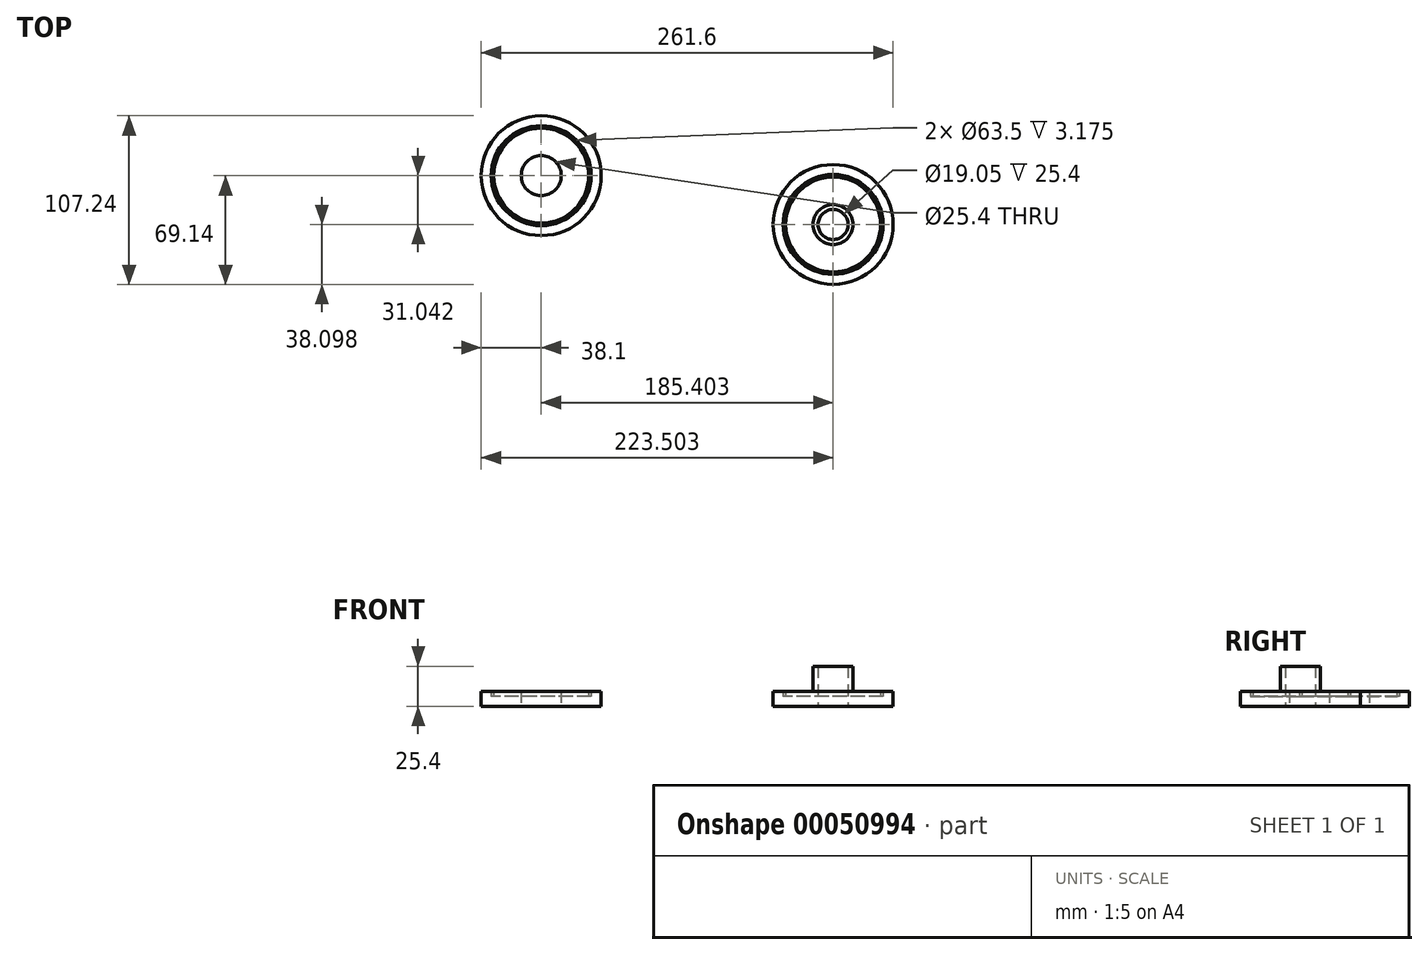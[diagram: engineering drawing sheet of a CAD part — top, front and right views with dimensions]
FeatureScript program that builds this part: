
annotation { "Feature Type Name" : "Feature", "Feature Type Description" : "" }
export const myFeature = defineFeature(function(context is Context, id is Id, definition is map)
    precondition{}
    {
        {
            var Q0;
            Q0=qCreatedBy(makeId("Top.planeOp"),FACE);
            var sketch = newSketch(context, id + "F0", { "sketchPlane" : qUnion([Q0])});
            skCircle(sketch, "E0", {"center": v(0, 0) * mm, "radius": 38.1 * mm});
            skCircle(sketch, "E1", {"center": v(0, 0) * mm, "radius": 31.75 * mm});
            skCircle(sketch, "E2", {"center": v(0, 0) * mm, "radius": 30.15 * mm});
            skCircle(sketch, "E3", {"center": v(0, 0) * mm, "radius": 12.7 * mm});
            skSolve(sketch);
        }
        {
            var Q0;
            Q0 = qSketchRegion(id + "F0", true);
            var Q1;
            Q1=makeQuery(id+"F0.imprint","IMPRINT",FACE,{"disambiguationData":[TD([[makeQuery(id+"F0.imprint","IMPRINT",EDGE,{"derivedFrom":sQuery(id+"F0.wireOp",EDGE,"E1")}),1.0]])]});
            var Q2;
            Q2=makeQuery(id+"F0.imprint","IMPRINT",FACE,{"disambiguationData":[TD([[makeQuery(id+"F0.imprint","IMPRINT",EDGE,{"derivedFrom":sQuery(id+"F0.wireOp",EDGE,"E2")}),1.0]])]});
            extrude(context, id + "F1", {"entities" : qUnion([Q0, Q1, Q2]), "depth" : 6.35 * mm});
        }
        {
            var Q0;
            Q0 = qSketchRegion(id + "F0", true);
            var Q1;
            Q1=makeQuery(id+"F0.imprint","IMPRINT",FACE,{"disambiguationData":[TD([[makeQuery(id+"F0.imprint","IMPRINT",EDGE,{"derivedFrom":sQuery(id+"F0.wireOp",EDGE,"E2")}),1.0]])]});
            extrude(context, id + "F2", {"entities" : qUnion([Q0, Q1]), "operationType" : NewBodyOperationType.ADD, "depth" : 9.52 * mm});
        }
        {
            var Q0;
            Q0=qCreatedBy(makeId("Top.planeOp"),FACE);
            var sketch = newSketch(context, id + "F3", { "sketchPlane" : qUnion([Q0])});
            skCircle(sketch, "E4", {"center": v(185.4, -31.04) * mm, "radius": 38.1 * mm});
            skCircle(sketch, "E5", {"center": v(185.4, -31.04) * mm, "radius": 31.75 * mm});
            skCircle(sketch, "E6", {"center": v(185.4, -31.04) * mm, "radius": 30.15 * mm});
            skCircle(sketch, "E7", {"center": v(185.4, -31.04) * mm, "radius": 12.7 * mm});
            skCircle(sketch, "E8", {"center": v(185.4, -31.04) * mm, "radius": 9.53 * mm});
            skSolve(sketch);
        }
        {
            var Q0;
            Q0=makeQuery(id+"F3.imprint","IMPRINT",FACE,{"disambiguationData":[TD([[makeQuery(id+"F3.imprint","IMPRINT",EDGE,{"derivedFrom":sQuery(id+"F3.wireOp",EDGE,"E5")}),1.0]])]});
            var Q1;
            Q1=makeQuery(id+"F3.imprint","IMPRINT",FACE,{"disambiguationData":[TD([[makeQuery(id+"F3.imprint","IMPRINT",EDGE,{"derivedFrom":sQuery(id+"F3.wireOp",EDGE,"E6")}),1.0]])]});
            var Q2;
            Q2=makeQuery(id+"F3.imprint","IMPRINT",FACE,{"disambiguationData":[TD([[makeQuery(id+"F3.imprint","IMPRINT",EDGE,{"derivedFrom":sQuery(id+"F3.wireOp",EDGE,"E4")}),1.0]])]});
            extrude(context, id + "F4", {"entities" : qUnion([Q0, Q1, Q2]), "depth" : 6.35 * mm});
        }
        {
            var Q0;
            Q0=makeQuery(id+"F3.imprint","IMPRINT",FACE,{"disambiguationData":[TD([[makeQuery(id+"F3.imprint","IMPRINT",EDGE,{"derivedFrom":sQuery(id+"F3.wireOp",EDGE,"E6")}),1.0]])]});
            var Q1;
            Q1=makeQuery(id+"F3.imprint","IMPRINT",FACE,{"disambiguationData":[TD([[makeQuery(id+"F3.imprint","IMPRINT",EDGE,{"derivedFrom":sQuery(id+"F3.wireOp",EDGE,"E4")}),1.0]])]});
            extrude(context, id + "F5", {"entities" : qUnion([Q0, Q1]), "operationType" : NewBodyOperationType.ADD, "depth" : 9.52 * mm});
        }
        {
            var Q0;
            Q0=makeQuery(id+"F3.imprint","IMPRINT",FACE,{"disambiguationData":[TD([[makeQuery(id+"F3.imprint","IMPRINT",EDGE,{"derivedFrom":sQuery(id+"F3.wireOp",EDGE,"E7")}),1.0]])]});
            extrude(context, id + "F6", {"entities" : qUnion([Q0]), "operationType" : NewBodyOperationType.ADD, "depth" : 25.4 * mm});
        }
    });
